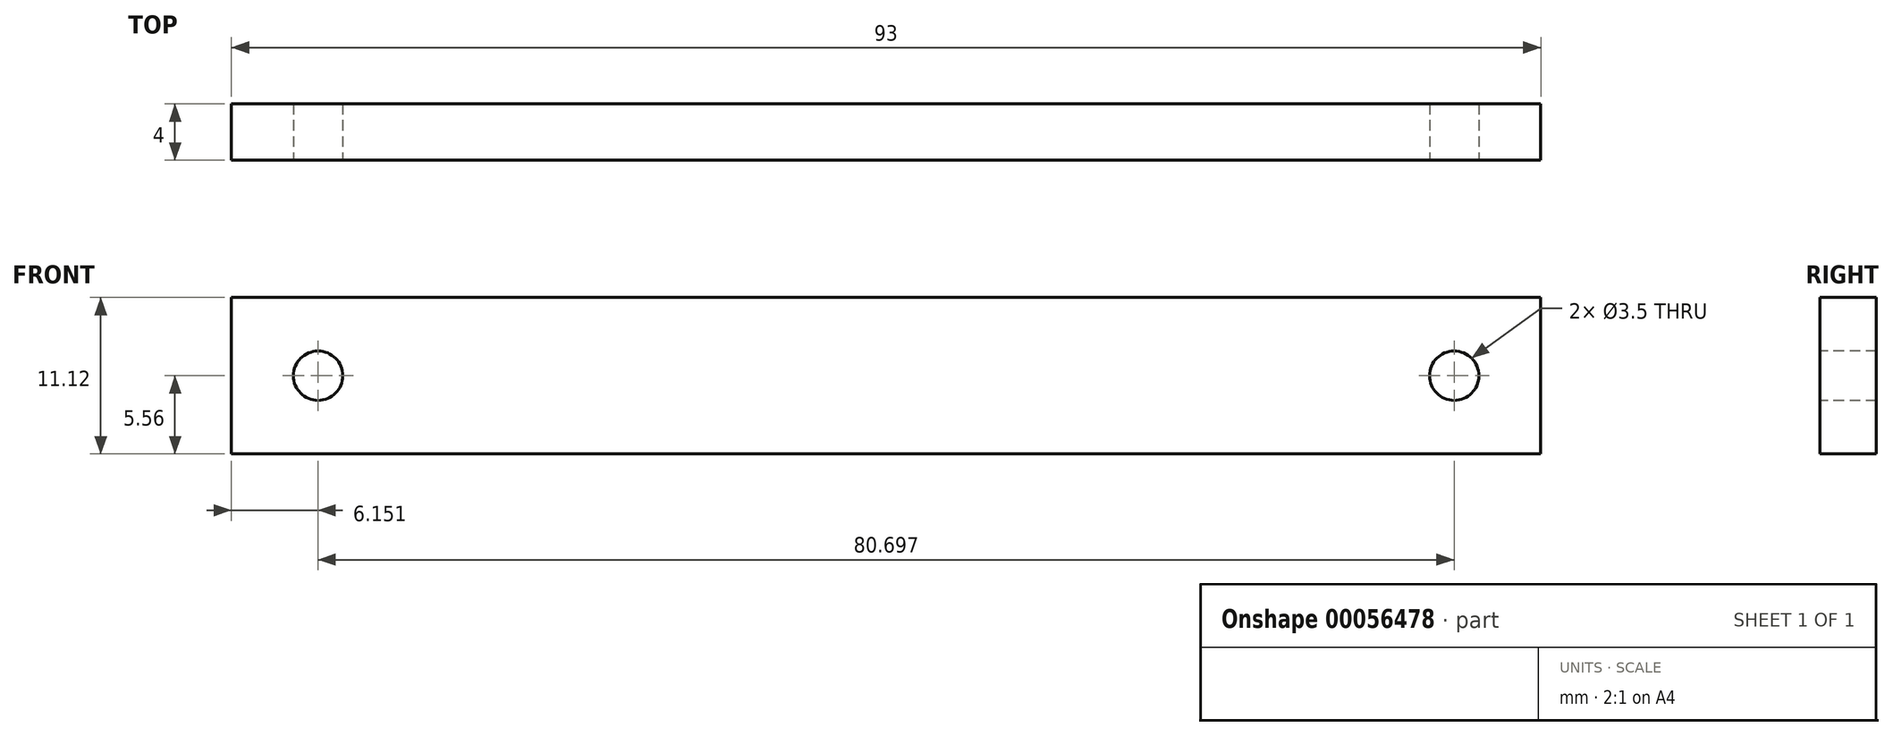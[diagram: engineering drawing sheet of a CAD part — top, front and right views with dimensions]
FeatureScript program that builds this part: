
annotation { "Feature Type Name" : "Feature", "Feature Type Description" : "" }
export const myFeature = defineFeature(function(context is Context, id is Id, definition is map)
    precondition{}
    {
        {
            var Q0;
            Q0=qCreatedBy(makeId("Front.planeOp"),FACE);
            var sketch = newSketch(context, id + "F0", { "sketchPlane" : qUnion([Q0])});
            skLineSegment(sketch, "E0.rect.bottom", {"start": v(46.5, 5.56) * mm, "end": v(-46.5, 5.56) * mm});
            skLineSegment(sketch, "E0.rect.top", {"start": v(46.5, -5.56) * mm, "end": v(-46.5, -5.56) * mm});
            skLineSegment(sketch, "E0.rect.left", {"start": v(46.5, 5.56) * mm, "end": v(46.5, -5.56) * mm});
            skLineSegment(sketch, "E0.rect.right", {"start": v(-46.5, 5.56) * mm, "end": v(-46.5, -5.56) * mm});
            skPoint(sketch, "E0.rect.middle", {"position": v(0, 0) * mm});
            skPoint(sketch, "E1", {"position": v(38.2, 116.76) * mm});
            skSolve(sketch);
        }
        {
            var Q0;
            Q0 = qSketchRegion(id + "F0", true);
            extrude(context, id + "F1", {"entities" : qUnion([Q0]), "depth" : 4 * mm});
        }
        {
            var Q0;
            Q0=makeQuery(id+"F1.opExtrude","CAP_FACE",FACE,{"disambiguationData":[OSD([sQuery(id+"F0.wireOp",EDGE,"E0.rect.bottom"),sQuery(id+"F0.wireOp",EDGE,"E0.rect.top"),sQuery(id+"F0.wireOp",EDGE,"E0.rect.left"),sQuery(id+"F0.wireOp",EDGE,"E0.rect.right")])],"isStart":false});
            var sketch = newSketch(context, id + "F2", { "sketchPlane" : qUnion([Q0])});
            skLineSegment(sketch, "E2", {"start": v(-46.5, 0) * mm, "end": v(-42.1, 0) * mm});
            skPoint(sketch, "E2.endSnap0", {"position": v(-46.5, 0) * mm});
            skPoint(sketch, "E3", {"position": v(-40.35, 0) * mm});
            skCircle(sketch, "E4", {"center": v(-40.35, 0) * mm, "radius": 1.75 * mm});
            skPoint(sketch, "E5.MirrorP", {"position": v(40.35, 0) * mm});
            skPoint(sketch, "E6.MirrorP", {"position": v(46.5, 0) * mm});
            skCircle(sketch, "E7.MirrorC", {"center": v(40.35, 0) * mm, "radius": 1.75 * mm});
            skLineSegment(sketch, "E8.MirrorCS", {"start": v(46.5, 0) * mm, "end": v(42.1, 0) * mm});
            skSolve(sketch);
        }
        {
            var Q0;
            Q0 = qSketchRegion(id + "F2", true);
            extrude(context, id + "F3", {"entities" : qUnion([Q0]), "operationType" : NewBodyOperationType.REMOVE, "oppositeDirection" : true, "depth" : 25 * mm});
        }
    });
